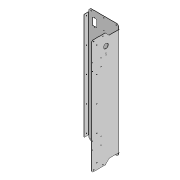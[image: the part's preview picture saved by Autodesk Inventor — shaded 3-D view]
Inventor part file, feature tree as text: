
AUTODESK INVENTOR PART (.ipt)
format: ipt  version: 2020 (Build 240168000, 168)  size: 586,752 bytes
history: native  units: mm
features: sketch x19, projected_geometry x11, other x10, hole x10, extrude x6, fillet x4, chamfer x3
ambient origin geometry x8: Origin, YZ Plane, XZ Plane, XY Plane, X Axis, Y Axis, Z Axis, Center Point
bodies: Body1 (feature_tree)
feature tree (63):
  other  "ソリッド1"
  other  "フランジ1"
  extrude  "押し出し2"  Depth=200.0mm
  hole  "穴2"  [1 undecoded]
  fillet  "フィレット1"  Radius=2.0mm
  other  "フランジ3"
  hole  "穴4"  [1 undecoded]
  hole  "穴5"  [1 undecoded]
  hole  "穴6"  [1 undecoded]
  hole  "穴7"  [1 undecoded]
  extrude  "押し出し3"  Depth=30.0mm TaperAngle=90.0deg
  hole  "穴8"  [1 undecoded]
  hole  "穴9"  [1 undecoded]
  extrude  "押し出し4"  Depth=2.0mm
  hole  "穴10"  [1 undecoded]
  chamfer  "面取り1"  Distance=47.0mm
  fillet  "フィレット2"  Radius=10.0mm
  extrude  "押し出し5"  Depth=20.594885mm
  hole  "穴11"  [1 undecoded]
  chamfer  "面取り2"  Distance=2.0mm
  chamfer  "面取り3"  Distance=1.0mm
  fillet  "フィレット3"  Radius=4.0mm
  extrude  "押し出し6"  Depth=2.0mm
  hole  "穴12"  [1 undecoded]
  extrude  "押し出し7"  Depth=8.0mm
  fillet  "フィレット4"  Radius=2.0mm
  sketch  "スケッチ1"
  other  "プレート1"
  sketch  "スケッチ2"
  other  "プレート2"
  other  "曲げ1"
  other  "コーナー1"
  sketch  "スケッチ6"
  sketch  "スケッチ7"
  projected_geometry  "投影ループ8"
  sketch  "スケッチ9"
  other  "プレート4"
  other  "曲げ3"
  other  "コーナー3"
  sketch  "スケッチ10"
  projected_geometry  "投影ループ9"
  sketch  "スケッチ11"
  projected_geometry  "投影ループ10"
  sketch  "スケッチ12"
  projected_geometry  "投影ループ11"
  sketch  "スケッチ13"
  sketch  "スケッチ14"
  projected_geometry  "投影ループ12"
  sketch  "スケッチ15"
  projected_geometry  "投影ループ13"
  sketch  "スケッチ16"
  projected_geometry  "投影ループ14"
  sketch  "スケッチ17"
  sketch  "スケッチ18"
  projected_geometry  "投影ループ15"
  sketch  "スケッチ19"
  sketch  "スケッチ20"
  projected_geometry  "投影ループ16"
  sketch  "スケッチ21"
  sketch  "スケッチ22"
  projected_geometry  "投影ループ17"
  sketch  "スケッチ23"
  projected_geometry  "投影ループ18"
note: 10 required parameter values undecoded (feature->parameter linkage not recoverable at this tier; creation-order binding heuristic only, values carry confidence <= 0.55)
